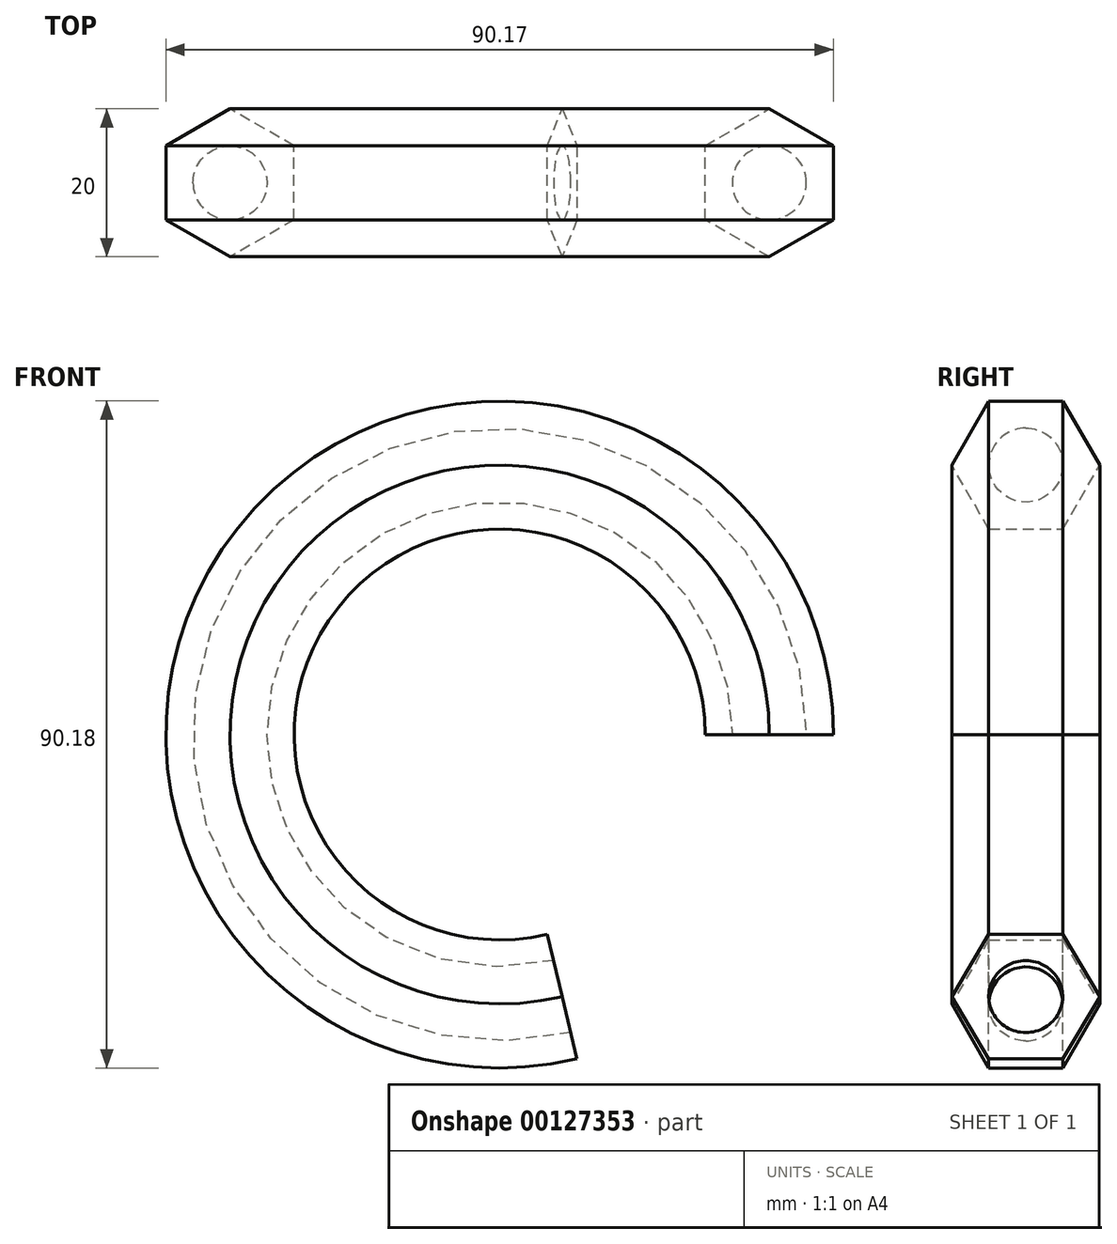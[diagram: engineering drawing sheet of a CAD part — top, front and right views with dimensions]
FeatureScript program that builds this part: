
annotation { "Feature Type Name" : "Feature", "Feature Type Description" : "" }
export const myFeature = defineFeature(function(context is Context, id is Id, definition is map)
    precondition{}
    {
        {
            var Q0;
            Q0=qCreatedBy(makeId("Top.planeOp"),FACE);
            var sketch = newSketch(context, id + "F0", { "sketchPlane" : qUnion([Q0])});
            skCircle(sketch, "E0.cCircle", {"center": v(0, 0) * mm, "radius": 8.66 * mm, "construction": true});
            skLineSegment(sketch, "E0.0", {"start": v(8.66, 5) * mm, "end": v(8.66, -5) * mm});
            skLineSegment(sketch, "E0.1", {"start": v(8.66, -5) * mm, "end": v(0, -10) * mm});
            skLineSegment(sketch, "E0.2", {"start": v(0, -10) * mm, "end": v(-8.66, -5) * mm});
            skLineSegment(sketch, "E0.3", {"start": v(-8.66, -5) * mm, "end": v(-8.66, 5) * mm});
            skLineSegment(sketch, "E0.4", {"start": v(-8.66, 5) * mm, "end": v(0, 10) * mm});
            skLineSegment(sketch, "E0.5", {"start": v(0, 10) * mm, "end": v(8.66, 5) * mm});
            skPoint(sketch, "E0.0.midPoint", {"position": v(8.66, 0) * mm});
            skCircle(sketch, "E1", {"center": v(0, 0) * mm, "radius": 5 * mm});
            skLineSegment(sketch, "E2", {"start": v(-36.43, 12.94) * mm, "end": v(-36.43, -37.05) * mm, "construction": true});
            skSolve(sketch);
        }
        {
            var Q0;
            Q0 = qSketchRegion(id + "F0", true);
            var Q1;
            Q1=sQuery(id+"F0.wireOp",EDGE,"E2");
            revolve(context, id + "F1", {"entities" : qUnion([Q0]), "axis" : qUnion([Q1]), "revolveType" : RevolveType.ONE_DIRECTION, "angle" : 283.41 * degree});
        }
    });
